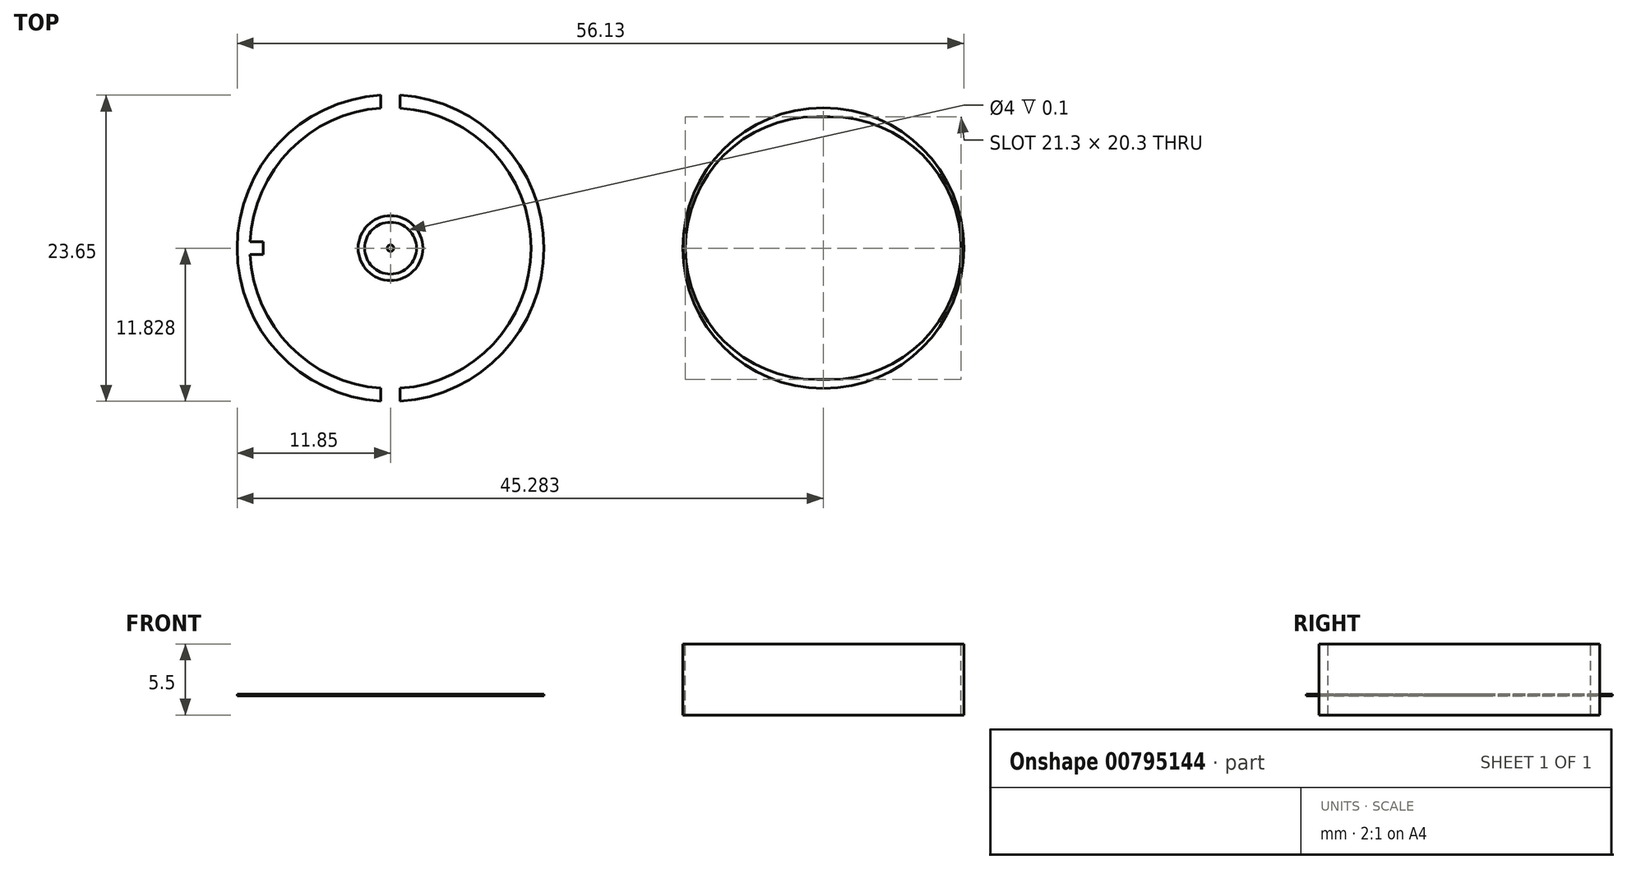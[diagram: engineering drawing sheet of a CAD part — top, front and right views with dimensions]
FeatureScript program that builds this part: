
annotation { "Feature Type Name" : "Feature", "Feature Type Description" : "" }
export const myFeature = defineFeature(function(context is Context, id is Id, definition is map)
    precondition{}
    {
        {
            var Q0;
            Q0=qCreatedBy(makeId("Top.planeOp"),FACE);
            var sketch = newSketch(context, id + "F0", { "sketchPlane" : qUnion([Q0])});
            skLineSegment(sketch, "E0.bottom", {"start": v(0, 0) * mm, "end": v(70, 0) * mm, "construction": true});
            skLineSegment(sketch, "E0.top", {"start": v(0, 100) * mm, "end": v(70, 100) * mm, "construction": true});
            skLineSegment(sketch, "E0.left", {"start": v(0, 0) * mm, "end": v(0, 100) * mm, "construction": true});
            skLineSegment(sketch, "E0.right", {"start": v(70, 0) * mm, "end": v(70, 100) * mm, "construction": true});
            skCircle(sketch, "E1", {"center": v(19.68, 82.24) * mm, "radius": 10.85 * mm});
            skCircle(sketch, "E2.0", {"center": v(19.68, 82.24) * mm, "radius": 11.85 * mm});
            skCircle(sketch, "E3", {"center": v(19.68, 82.24) * mm, "radius": 0.25 * mm});
            skCircle(sketch, "E4", {"center": v(19.68, 82.24) * mm, "radius": 2 * mm});
            skCircle(sketch, "E5", {"center": v(19.68, 82.24) * mm, "radius": 2.5 * mm});
            skLineSegment(sketch, "E6.bottom", {"start": v(8.84, 81.74) * mm, "end": v(9.84, 81.74) * mm});
            skLineSegment(sketch, "E6.top", {"start": v(8.84, 82.74) * mm, "end": v(9.84, 82.74) * mm});
            skLineSegment(sketch, "E6.left", {"start": v(8.84, 81.74) * mm, "end": v(8.84, 82.74) * mm});
            skLineSegment(sketch, "E6.right", {"start": v(9.84, 81.74) * mm, "end": v(9.84, 82.74) * mm});
            skLineSegment(sketch, "E7.bottom", {"start": v(20.43, 92.99) * mm, "end": v(18.93, 92.99) * mm});
            skLineSegment(sketch, "E7.top", {"start": v(20.43, 94.49) * mm, "end": v(18.93, 94.49) * mm});
            skLineSegment(sketch, "E7.left", {"start": v(20.43, 92.99) * mm, "end": v(20.43, 94.49) * mm});
            skLineSegment(sketch, "E7.right", {"start": v(18.93, 92.99) * mm, "end": v(18.93, 94.49) * mm});
            skPoint(sketch, "E7.middle", {"position": v(19.68, 93.74) * mm});
            skLineSegment(sketch, "E8.bottom", {"start": v(20.43, 69.99) * mm, "end": v(18.93, 69.99) * mm});
            skLineSegment(sketch, "E8.top", {"start": v(20.43, 71.49) * mm, "end": v(18.93, 71.49) * mm});
            skLineSegment(sketch, "E8.left", {"start": v(20.43, 69.99) * mm, "end": v(20.43, 71.49) * mm});
            skLineSegment(sketch, "E8.right", {"start": v(18.93, 69.99) * mm, "end": v(18.93, 71.49) * mm});
            skPoint(sketch, "E8.middle", {"position": v(19.68, 70.74) * mm});
            skCircle(sketch, "E9", {"center": v(19.68, 82.24) * mm, "radius": 11.5 * mm, "construction": true});
            skCircle(sketch, "E10", {"center": v(53.11, 82.24) * mm, "radius": 10.85 * mm});
            skLineSegment(sketch, "E11", {"start": v(52.61, 82.24) * mm, "end": v(53.61, 82.24) * mm, "construction": true});
            skArc(sketch, "E12.0.startCap", {"start": v(52.61, 72.09) * mm, "mid": v(42.46, 82.24) * mm, "end": v(52.61, 92.39) * mm});
            skArc(sketch, "E12.0.endCap", {"start": v(53.61, 92.39) * mm, "mid": v(63.76, 82.24) * mm, "end": v(53.61, 72.09) * mm});
            skLineSegment(sketch, "E12.0.left", {"start": v(52.61, 92.39) * mm, "end": v(53.61, 92.39) * mm});
            skLineSegment(sketch, "E12.0.right", {"start": v(52.61, 72.09) * mm, "end": v(53.61, 72.09) * mm});
            skSolve(sketch);
        }
        {
            var Q0;
            Q0=makeQuery(id+"F0.imprint","IMPRINT",FACE,{"disambiguationData":[TD([[makeQuery(id+"F0.imprint","IMPRINT",EDGE,{"derivedFrom":sQuery(id+"F0.wireOp",EDGE,"E4")}),-1.0]])]});
            extrude(context, id + "F1", {"entities" : qUnion([Q0]), "depth" : .1 * mm, "offsetDistance" : 25 * mm});
        }
        {
            var Q0;
            {var subQ5=sQuery(id+"F0.wireOp",EDGE,"E7.right");var subQ6=sQuery(id+"F0.wireOp",EDGE,"E2.0");var subQ7=makeQuery(id+"F0.imprint","INTERSECT",VERTEX,{"derivedFrom":[subQ6,subQ5]});Q0=makeQuery(id+"F0.imprint","IMPRINT",FACE,{"disambiguationData":[TD([[makeQuery(id+"F0.imprint","IMPRINT",EDGE,{"disambiguationData":[TD([[subQ7,-1.0]])],"derivedFrom":subQ6}),1.0]])]});}
            var Q1;
            {var subQ0=sQuery(id+"F0.wireOp",EDGE,"E7.left");var subQ1=sQuery(id+"F0.wireOp",EDGE,"E1");var subQ2=makeQuery(id+"F0.imprint","INTERSECT",VERTEX,{"derivedFrom":[subQ1,subQ0]});Q1=makeQuery(id+"F0.imprint","IMPRINT",FACE,{"disambiguationData":[TD([[makeQuery(id+"F0.imprint","IMPRINT",EDGE,{"disambiguationData":[TD([[subQ2,1.0]])],"derivedFrom":subQ1}),-1.0]])]});}
            var Q2;
            Q2=makeQuery(id+"F0.imprint","IMPRINT",FACE,{"disambiguationData":[TD([[makeQuery(id+"F0.imprint","IMPRINT",EDGE,{"derivedFrom":sQuery(id+"F0.wireOp",EDGE,"E6.bottom")}),1.0]])]});
            var Q3;
            {var subQ0=sQuery(id+"F0.wireOp",EDGE,"E6.left");Q3=makeQuery(id+"F0.imprint","IMPRINT",FACE,{"disambiguationData":[TD([[makeQuery(id+"F0.imprint","IMPRINT",EDGE,{"derivedFrom":subQ0}),1.0]])]});}
            extrude(context, id + "F2", {"entities" : qUnion([Q0, Q1, Q2, Q3]), "depth" : .1 * mm, "offsetDistance" : 25 * mm});
        }
        {
            var Q0;
            Q0=makeQuery(id+"F0.imprint","IMPRINT",FACE,{"disambiguationData":[TD([[makeQuery(id+"F0.imprint","IMPRINT",EDGE,{"derivedFrom":sQuery(id+"F0.wireOp",EDGE,"E3")}),1.0]])]});
            extrude(context, id + "F3", {"entities" : qUnion([Q0]), "depth" : .1 * mm, "offsetDistance" : 25 * mm});
        }
        {
            var Q0;
            Q0=makeQuery(id+"F0.imprint","IMPRINT",FACE,{"disambiguationData":[TD([[makeQuery(id+"F0.imprint","IMPRINT",EDGE,{"derivedFrom":sQuery(id+"F0.wireOp",EDGE,"E10")}),1.0]])]});
            var Q1;
            Q1=makeQuery(id+"F0.imprint","IMPRINT",FACE,{"disambiguationData":[TD([[makeQuery(id+"F0.imprint","IMPRINT",EDGE,{"derivedFrom":sQuery(id+"F0.wireOp",EDGE,"E12.0.startCap")}),-1.0]])]});
            extrude(context, id + "F4", {"entities" : qUnion([Q0, Q1]), "oppositeDirection" : true, "depth" : 1.5 * mm, "offsetDistance" : 25 * mm});
        }
        {
            var Q0;
            Q0=makeQuery(id+"F0.imprint","IMPRINT",FACE,{"disambiguationData":[TD([[makeQuery(id+"F0.imprint","IMPRINT",EDGE,{"derivedFrom":sQuery(id+"F0.wireOp",EDGE,"E10")}),1.0]])]});
            extrude(context, id + "F5", {"entities" : qUnion([Q0]), "operationType" : NewBodyOperationType.ADD, "depth" : 4 * mm, "offsetDistance" : 25 * mm});
        }
    });
